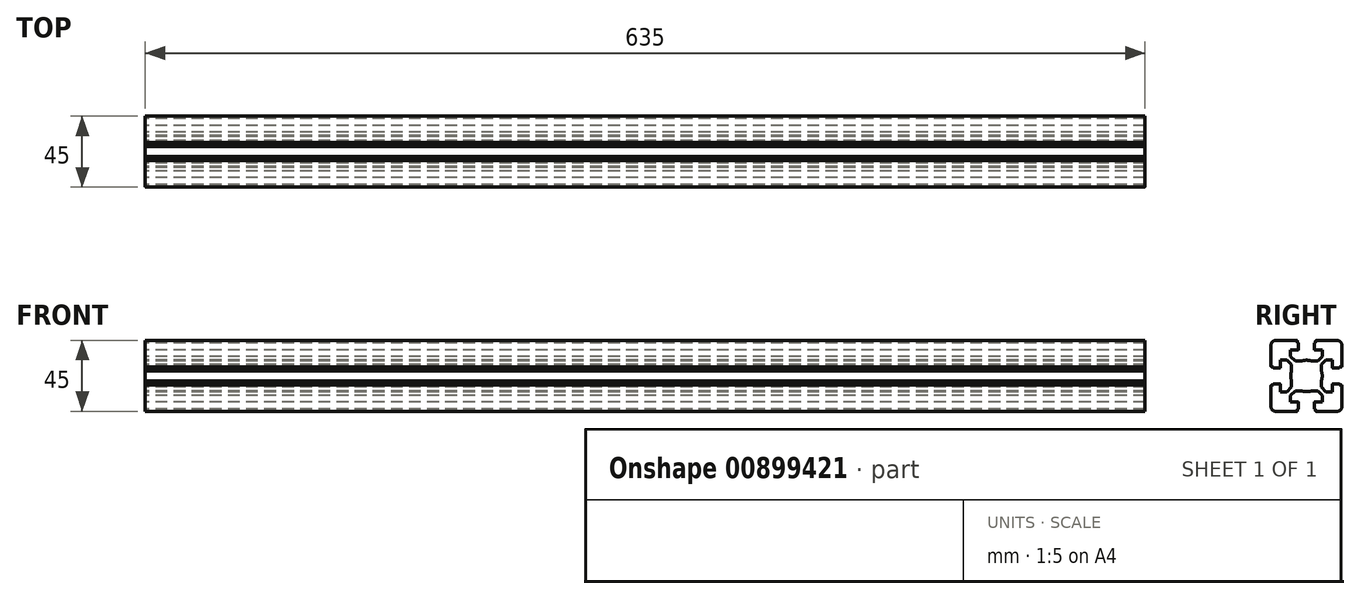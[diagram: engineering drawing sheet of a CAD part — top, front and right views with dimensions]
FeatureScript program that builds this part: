
annotation { "Feature Type Name" : "Feature", "Feature Type Description" : "" }
export const myFeature = defineFeature(function(context is Context, id is Id, definition is map)
    precondition{}
    {
        {
            var Q0;
            Q0=qCreatedBy(makeId("Right.planeOp"),FACE);
            var sketch = newSketch(context, id + "F0", { "sketchPlane" : qUnion([Q0])});
            skLineSegment(sketch, "E0", {"start": v(-20.09, -10.29) * mm, "end": v(-21.29, -10.29) * mm});
            skArc(sketch, "E1", {"start": v(-21.29, -10.29) * mm, "mid": v(-21.5, -10.38) * mm, "end": v(-21.59, -10.59) * mm});
            skLineSegment(sketch, "E2", {"start": v(-21.59, -10.59) * mm, "end": v(-21.59, -23.99) * mm});
            skArc(sketch, "E3", {"start": v(-21.59, -23.99) * mm, "mid": v(-20.7, -26.11) * mm, "end": v(-18.59, -26.99) * mm});
            skLineSegment(sketch, "E4", {"start": v(-18.59, -26.99) * mm, "end": v(-5.19, -26.99) * mm});
            skArc(sketch, "E5", {"start": v(-5.19, -26.99) * mm, "mid": v(-4.98, -26.9) * mm, "end": v(-4.89, -26.69) * mm});
            skLineSegment(sketch, "E6", {"start": v(-4.89, -26.69) * mm, "end": v(-4.89, -25.49) * mm});
            skLineSegment(sketch, "E7", {"start": v(-4.89, -25.49) * mm, "end": v(-4.39, -25.49) * mm});
            skArc(sketch, "E8", {"start": v(-4.39, -25.49) * mm, "mid": v(-4.18, -25.4) * mm, "end": v(-4.09, -25.19) * mm});
            skLineSegment(sketch, "E9", {"start": v(-4.09, -25.19) * mm, "end": v(-4.09, -21.29) * mm});
            skArc(sketch, "E10", {"start": v(-4.09, -21.29) * mm, "mid": v(-4.18, -21.08) * mm, "end": v(-4.39, -20.99) * mm});
            skLineSegment(sketch, "E11", {"start": v(-4.39, -20.99) * mm, "end": v(-9.14, -20.99) * mm});
            skLineSegment(sketch, "E12", {"start": v(-9.14, -20.99) * mm, "end": v(-9.14, -16.88) * mm});
            skLineSegment(sketch, "E13", {"start": v(-9.14, -16.88) * mm, "end": v(-6.25, -13.99) * mm});
            skLineSegment(sketch, "E14", {"start": v(-6.25, -13.99) * mm, "end": v(-2.21, -13.99) * mm});
            skArc(sketch, "E15", {"start": v(-2.21, -13.99) * mm, "mid": v(0.91, -14.49) * mm, "end": v(4.03, -13.99) * mm});
            skLineSegment(sketch, "E16", {"start": v(-20.09, -10.29) * mm, "end": v(-20.09, -9.79) * mm});
            skArc(sketch, "E17", {"start": v(-20.09, -9.79) * mm, "mid": v(-20, -9.58) * mm, "end": v(-19.79, -9.49) * mm});
            skLineSegment(sketch, "E18", {"start": v(-19.79, -9.49) * mm, "end": v(-15.89, -9.49) * mm});
            skArc(sketch, "E19", {"start": v(-15.89, -9.49) * mm, "mid": v(-15.68, -9.58) * mm, "end": v(-15.59, -9.79) * mm});
            skLineSegment(sketch, "E20", {"start": v(-15.59, -9.79) * mm, "end": v(-15.59, -14.54) * mm});
            skLineSegment(sketch, "E21", {"start": v(-15.59, -14.54) * mm, "end": v(-11.48, -14.54) * mm});
            skLineSegment(sketch, "E22", {"start": v(-11.48, -14.54) * mm, "end": v(-8.59, -11.65) * mm});
            skLineSegment(sketch, "E23", {"start": v(-8.59, -11.65) * mm, "end": v(-8.59, -7.61) * mm});
            skLineSegment(sketch, "E24", {"start": v(29.82, -4.49) * mm, "end": v(-31.05, -4.49) * mm});
            skLineSegment(sketch, "E25.MirrorCS", {"start": v(6.71, -25.49) * mm, "end": v(6.21, -25.49) * mm});
            skArc(sketch, "E26.MirrorCS", {"start": v(7.01, -26.99) * mm, "mid": v(6.8, -26.9) * mm, "end": v(6.71, -26.69) * mm});
            skLineSegment(sketch, "E27.MirrorCS", {"start": v(10.41, -11.65) * mm, "end": v(10.41, -7.61) * mm});
            skArc(sketch, "E28.MirrorCS", {"start": v(6.21, -25.49) * mm, "mid": v(6, -25.4) * mm, "end": v(5.91, -25.19) * mm});
            skLineSegment(sketch, "E29.MirrorCS", {"start": v(6.71, -26.69) * mm, "end": v(6.71, -25.49) * mm});
            skArc(sketch, "E30.MirrorCS", {"start": v(5.91, -21.29) * mm, "mid": v(6, -21.08) * mm, "end": v(6.21, -20.99) * mm});
            skLineSegment(sketch, "E31.MirrorCS", {"start": v(10.96, -16.88) * mm, "end": v(8.07, -13.99) * mm});
            skLineSegment(sketch, "E32.MirrorCS", {"start": v(13.3, -14.54) * mm, "end": v(10.41, -11.65) * mm});
            skLineSegment(sketch, "E33.MirrorCS", {"start": v(17.41, -14.54) * mm, "end": v(13.3, -14.54) * mm});
            skLineSegment(sketch, "E34.MirrorCS", {"start": v(17.41, -9.79) * mm, "end": v(17.41, -14.54) * mm});
            skLineSegment(sketch, "E35.MirrorCS", {"start": v(6.21, -20.99) * mm, "end": v(10.96, -20.99) * mm});
            skLineSegment(sketch, "E36.MirrorCS", {"start": v(8.07, -13.99) * mm, "end": v(4.03, -13.99) * mm});
            skArc(sketch, "E37.MirrorCS", {"start": v(4.03, -13.99) * mm, "mid": v(0.91, -14.49) * mm, "end": v(-2.21, -13.99) * mm});
            skLineSegment(sketch, "E38.MirrorCS", {"start": v(10.96, -20.99) * mm, "end": v(10.96, -16.88) * mm});
            skLineSegment(sketch, "E39.MirrorCS", {"start": v(5.91, -25.19) * mm, "end": v(5.91, -21.29) * mm});
            skArc(sketch, "E40.MirrorCS", {"start": v(23.41, -23.99) * mm, "mid": v(22.53, -26.11) * mm, "end": v(20.41, -26.99) * mm});
            skLineSegment(sketch, "E41.MirrorCS", {"start": v(20.41, -26.99) * mm, "end": v(7.01, -26.99) * mm});
            skLineSegment(sketch, "E42.MirrorCS", {"start": v(23.41, -10.59) * mm, "end": v(23.41, -23.99) * mm});
            skArc(sketch, "E43.MirrorCS", {"start": v(17.71, -9.49) * mm, "mid": v(17.5, -9.58) * mm, "end": v(17.41, -9.79) * mm});
            skArc(sketch, "E44.MirrorCS", {"start": v(23.11, -10.29) * mm, "mid": v(23.32, -10.38) * mm, "end": v(23.41, -10.59) * mm});
            skLineSegment(sketch, "E45.MirrorCS", {"start": v(21.91, -10.29) * mm, "end": v(21.91, -9.79) * mm});
            skLineSegment(sketch, "E46.MirrorCS", {"start": v(21.91, -10.29) * mm, "end": v(23.11, -10.29) * mm});
            skArc(sketch, "E47.MirrorCS", {"start": v(21.91, -9.79) * mm, "mid": v(21.82, -9.58) * mm, "end": v(21.61, -9.49) * mm});
            skLineSegment(sketch, "E48.MirrorCS", {"start": v(21.61, -9.49) * mm, "end": v(17.71, -9.49) * mm});
            skLineSegment(sketch, "E49.MirrorCS", {"start": v(6.71, 16.51) * mm, "end": v(6.21, 16.51) * mm});
            skArc(sketch, "E50.MirrorCS", {"start": v(-4.39, 16.51) * mm, "mid": v(-4.18, 16.42) * mm, "end": v(-4.09, 16.21) * mm});
            skLineSegment(sketch, "E51.MirrorCS", {"start": v(-4.89, 16.51) * mm, "end": v(-4.39, 16.51) * mm});
            skArc(sketch, "E52.MirrorCS", {"start": v(5.91, 12.31) * mm, "mid": v(6, 12.1) * mm, "end": v(6.21, 12.01) * mm});
            skLineSegment(sketch, "E53.MirrorCS", {"start": v(6.71, 17.71) * mm, "end": v(6.71, 16.51) * mm});
            skLineSegment(sketch, "E54.MirrorCS", {"start": v(-4.89, 17.71) * mm, "end": v(-4.89, 16.51) * mm});
            skArc(sketch, "E55.MirrorCS", {"start": v(-5.19, 18.01) * mm, "mid": v(-4.98, 17.92) * mm, "end": v(-4.89, 17.71) * mm});
            skArc(sketch, "E56.MirrorCS", {"start": v(-4.09, 12.31) * mm, "mid": v(-4.18, 12.1) * mm, "end": v(-4.39, 12.01) * mm});
            skArc(sketch, "E57.MirrorCS", {"start": v(7.01, 18.01) * mm, "mid": v(6.8, 17.92) * mm, "end": v(6.71, 17.71) * mm});
            skArc(sketch, "E58.MirrorCS", {"start": v(6.21, 16.51) * mm, "mid": v(6, 16.42) * mm, "end": v(5.91, 16.21) * mm});
            skArc(sketch, "E59.MirrorCS", {"start": v(23.11, 1.31) * mm, "mid": v(23.32, 1.4) * mm, "end": v(23.41, 1.61) * mm});
            skLineSegment(sketch, "E60.MirrorCS", {"start": v(21.91, 1.31) * mm, "end": v(21.91, 0.81) * mm});
            skArc(sketch, "E61.MirrorCS", {"start": v(-15.89, 0.51) * mm, "mid": v(-15.68, 0.6) * mm, "end": v(-15.59, 0.81) * mm});
            skArc(sketch, "E62.MirrorCS", {"start": v(-21.29, 1.31) * mm, "mid": v(-21.5, 1.4) * mm, "end": v(-21.59, 1.61) * mm});
            skArc(sketch, "E63.MirrorCS", {"start": v(17.71, 0.51) * mm, "mid": v(17.5, 0.6) * mm, "end": v(17.41, 0.81) * mm});
            skArc(sketch, "E64.MirrorCS", {"start": v(21.91, 0.81) * mm, "mid": v(21.82, 0.6) * mm, "end": v(21.61, 0.51) * mm});
            skLineSegment(sketch, "E65.MirrorCS", {"start": v(21.91, 1.31) * mm, "end": v(23.11, 1.31) * mm});
            skArc(sketch, "E66.MirrorCS", {"start": v(14.31, 5.31) * mm, "mid": v(14.1, 5.4) * mm, "end": v(14.01, 5.61) * mm});
            skArc(sketch, "E67.MirrorCS", {"start": v(-20.09, 0.81) * mm, "mid": v(-20, 0.6) * mm, "end": v(-19.79, 0.51) * mm});
            skLineSegment(sketch, "E68.MirrorCS", {"start": v(-20.09, 1.31) * mm, "end": v(-21.29, 1.31) * mm});
            skLineSegment(sketch, "E69.MirrorCS", {"start": v(-20.09, 1.31) * mm, "end": v(-20.09, 0.81) * mm});
            skLineSegment(sketch, "E70.MirrorCS", {"start": v(8.07, 5.01) * mm, "end": v(4.03, 5.01) * mm});
            skLineSegment(sketch, "E71.MirrorCS", {"start": v(-4.09, 16.21) * mm, "end": v(-4.09, 12.31) * mm});
            skLineSegment(sketch, "E72.MirrorCS", {"start": v(-9.14, 12.01) * mm, "end": v(-9.14, 7.9) * mm});
            skLineSegment(sketch, "E73.MirrorCS", {"start": v(-15.59, 5.56) * mm, "end": v(-11.48, 5.56) * mm});
            skLineSegment(sketch, "E74.MirrorCS", {"start": v(-4.39, 12.01) * mm, "end": v(-9.14, 12.01) * mm});
            skLineSegment(sketch, "E75.MirrorCS", {"start": v(-9.14, 7.9) * mm, "end": v(-6.25, 5.01) * mm});
            skLineSegment(sketch, "E76.MirrorCS", {"start": v(10.96, 12.01) * mm, "end": v(10.96, 7.9) * mm});
            skArc(sketch, "E77.MirrorCS", {"start": v(-21.59, 15.01) * mm, "mid": v(-20.7, 17.13) * mm, "end": v(-18.59, 18.01) * mm});
            skLineSegment(sketch, "E78.MirrorCS", {"start": v(23.41, 1.61) * mm, "end": v(23.41, 15.01) * mm});
            skLineSegment(sketch, "E79.MirrorCS", {"start": v(13.3, 5.56) * mm, "end": v(10.41, 2.67) * mm});
            skLineSegment(sketch, "E80.MirrorCS", {"start": v(-8.59, 2.67) * mm, "end": v(-8.59, -1.37) * mm});
            skLineSegment(sketch, "E81.MirrorCS", {"start": v(-15.59, 0.81) * mm, "end": v(-15.59, 5.56) * mm});
            skLineSegment(sketch, "E82.MirrorCS", {"start": v(10.41, 2.67) * mm, "end": v(10.41, -1.37) * mm});
            skLineSegment(sketch, "E83.MirrorCS", {"start": v(-18.59, 18.01) * mm, "end": v(-5.19, 18.01) * mm});
            skLineSegment(sketch, "E84.MirrorCS", {"start": v(10.96, 7.9) * mm, "end": v(8.07, 5.01) * mm});
            skLineSegment(sketch, "E85.MirrorCS", {"start": v(17.41, 5.56) * mm, "end": v(13.3, 5.56) * mm});
            skArc(sketch, "E86.MirrorCS", {"start": v(23.41, 15.01) * mm, "mid": v(22.53, 17.13) * mm, "end": v(20.41, 18.01) * mm});
            skLineSegment(sketch, "E87.MirrorCS", {"start": v(5.91, 16.21) * mm, "end": v(5.91, 12.31) * mm});
            skLineSegment(sketch, "E88.MirrorCS", {"start": v(17.41, 0.81) * mm, "end": v(17.41, 5.56) * mm});
            skLineSegment(sketch, "E89.MirrorCS", {"start": v(-11.48, 5.56) * mm, "end": v(-8.59, 2.67) * mm});
            skLineSegment(sketch, "E90.MirrorCS", {"start": v(-6.25, 5.01) * mm, "end": v(-2.21, 5.01) * mm});
            skLineSegment(sketch, "E91.MirrorCS", {"start": v(-21.59, 1.61) * mm, "end": v(-21.59, 15.01) * mm});
            skArc(sketch, "E92.MirrorCS", {"start": v(4.03, 5.01) * mm, "mid": v(0.91, 5.51) * mm, "end": v(-2.21, 5.01) * mm});
            skLineSegment(sketch, "E93.MirrorCS", {"start": v(6.21, 12.01) * mm, "end": v(10.96, 12.01) * mm});
            skArc(sketch, "E94.MirrorCS", {"start": v(-2.21, 5.01) * mm, "mid": v(0.91, 5.51) * mm, "end": v(4.03, 5.01) * mm});
            skLineSegment(sketch, "E95.MirrorCS", {"start": v(20.41, 18.01) * mm, "end": v(7.01, 18.01) * mm});
            skLineSegment(sketch, "E96.MirrorCS", {"start": v(-19.79, 0.51) * mm, "end": v(-15.89, 0.51) * mm});
            skLineSegment(sketch, "E97.MirrorCS", {"start": v(21.61, 0.51) * mm, "end": v(17.71, 0.51) * mm});
            skLineSegment(sketch, "E98.MirrorCS", {"start": v(0.91, -27.65) * mm, "end": v(0.91, 19.82) * mm});
            skArc(sketch, "E99", {"start": v(-8.59, -1.37) * mm, "mid": v(-9.09, -4.49) * mm, "end": v(-8.59, -7.61) * mm});
            skArc(sketch, "E100", {"start": v(10.41, -7.61) * mm, "mid": v(10.91, -4.49) * mm, "end": v(10.41, -1.37) * mm});
            skSolve(sketch);
        }
        {
            var Q0;
            Q0=qSketchRegion(id+"F0",true);
            extrude(context, id + "F1", {"entities" : qUnion([Q0]), "depth" : 635 * mm, "offsetDistance" : 25.4 * mm});
        }
    });
